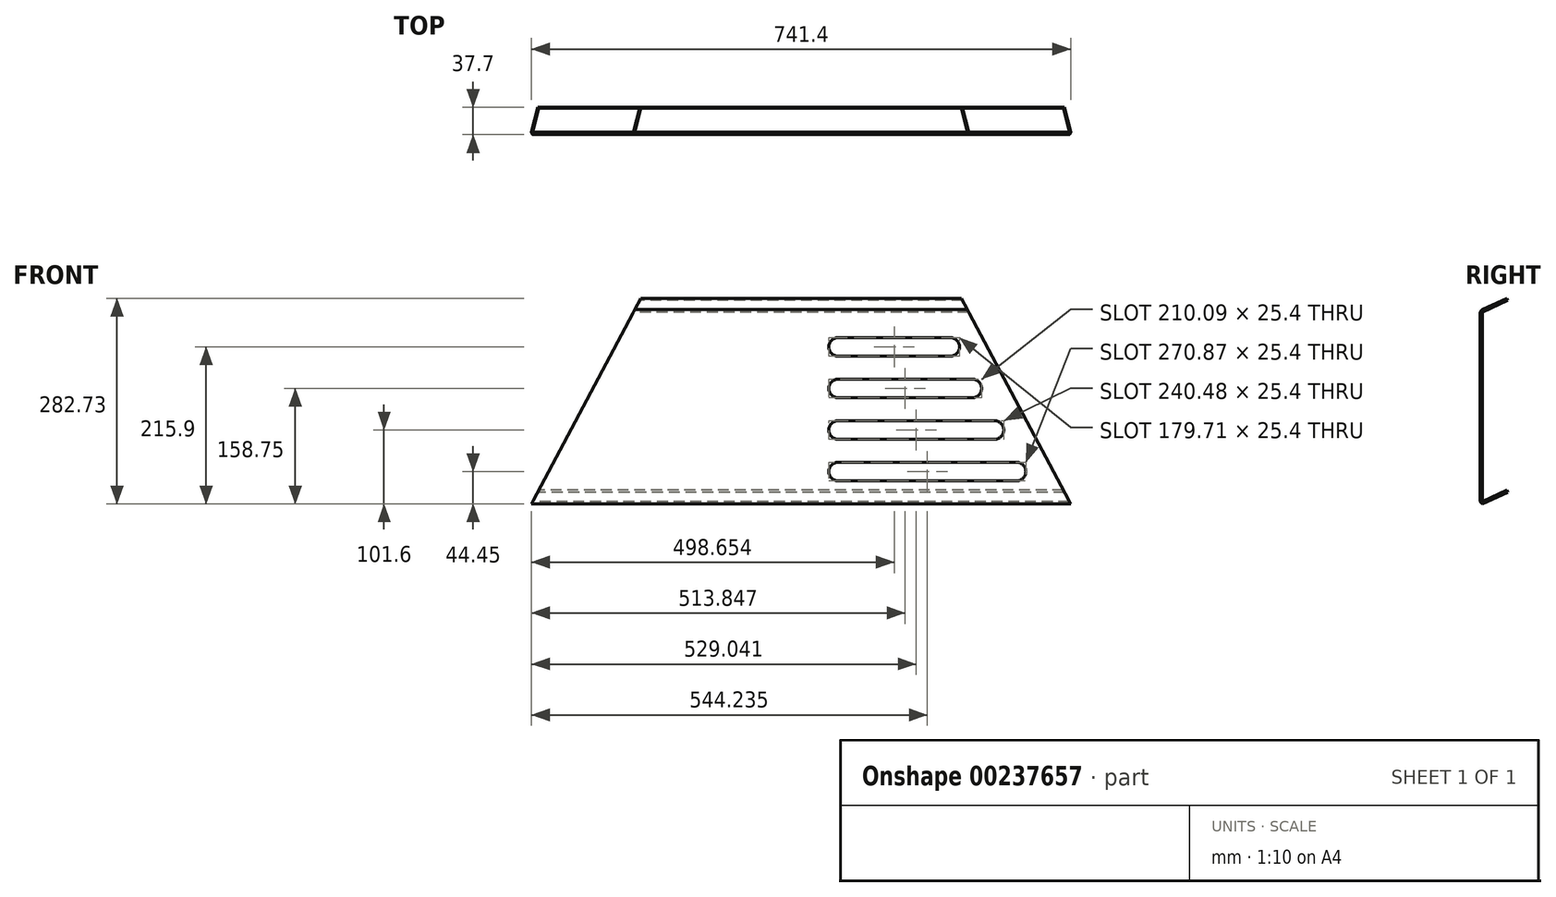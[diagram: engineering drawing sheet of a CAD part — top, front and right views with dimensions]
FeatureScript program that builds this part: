
annotation { "Feature Type Name" : "Feature", "Feature Type Description" : "" }
export const myFeature = defineFeature(function(context is Context, id is Id, definition is map)
    precondition{}
    {
        {
            var Q0;
            Q0=qCreatedBy(makeId("Front.planeOp"),FACE);
            var sketch = newSketch(context, id + "F0", { "sketchPlane" : qUnion([Q0])});
            skLineSegment(sketch, "E0", {"start": v(-228.6, 267.26) * mm, "end": v(228.6, 267.26) * mm});
            skLineSegment(sketch, "E1", {"start": v(228.6, 267.26) * mm, "end": v(370.7, 0) * mm});
            skLineSegment(sketch, "E2", {"start": v(370.7, 0) * mm, "end": v(-370.7, 0) * mm});
            skLineSegment(sketch, "E3", {"start": v(-370.7, 0) * mm, "end": v(-228.6, 267.26) * mm});
            skSolve(sketch);
        }
        {
            var Q0;
            Q0 = qSketchRegion(id + "F0", true);
            extrude(context, id + "F1", {"entities" : qUnion([Q0]), "depth" : 3.17 * mm});
        }
        {
            var Q0;
            Q0=qCreatedBy(makeId("Right.planeOp"),FACE);
            var sketch = newSketch(context, id + "F2", { "sketchPlane" : qUnion([Q0])});
            skLineSegment(sketch, "E4", {"start": v(0, 0) * mm, "end": v(34.53, 16.1) * mm});
            skLineSegment(sketch, "E5", {"start": v(34.53, 16.1) * mm, "end": v(33.19, 18.98) * mm});
            skLineSegment(sketch, "E6", {"start": v(33.19, 18.98) * mm, "end": v(0, 3.5) * mm});
            skLineSegment(sketch, "E7", {"start": v(0, 0) * mm, "end": v(0, 3.5) * mm});
            skLineSegment(sketch, "E8", {"start": v(0, 263.76) * mm, "end": v(34.53, 279.86) * mm});
            skLineSegment(sketch, "E9", {"start": v(34.53, 279.86) * mm, "end": v(33.19, 282.73) * mm});
            skLineSegment(sketch, "E10", {"start": v(33.19, 282.73) * mm, "end": v(0, 267.26) * mm});
            skLineSegment(sketch, "E11", {"start": v(0, 263.76) * mm, "end": v(0, 267.26) * mm});
            skSolve(sketch);
        }
        {
            var Q0;
            Q0=makeQuery(id+"F2.imprint","IMPRINT",FACE,{"disambiguationData":[TD([[makeQuery(id+"F2.imprint","IMPRINT",EDGE,{"derivedFrom":sQuery(id+"F2.wireOp",EDGE,"E4")}),1.0]])]});
            var Q1;
            Q1=makeQuery(id+"F2.imprint","IMPRINT",FACE,{"disambiguationData":[TD([[makeQuery(id+"F2.imprint","IMPRINT",EDGE,{"derivedFrom":sQuery(id+"F2.wireOp",EDGE,"E8")}),1.0]])]});
            var Q2;
            Q2=makeQuery(id+"F1.opExtrude","SWEPT_FACE",FACE,{"disambiguationData":[OSD([sQuery(id+"F0.wireOp",EDGE,"E1")])]});
            var Q3;
            Q3=makeQuery(id+"F1.opExtrude","SWEPT_FACE",FACE,{"disambiguationData":[OSD([sQuery(id+"F0.wireOp",EDGE,"E3")])]});
            extrude(context, id + "F3", {"entities" : qUnion([Q0, Q1]), "operationType" : NewBodyOperationType.ADD, "endBound" : BoundingType.UP_TO_SURFACE, "endBoundEntityFace" : qUnion([Q2]), "depth" : 25.4 * mm, "hasSecondDirection" : true, "secondDirectionBound" : SecondDirectionBoundingType.UP_TO_SURFACE, "secondDirectionOppositeDirection" : true, "secondDirectionBoundEntityFace" : qUnion([Q3]), "secondDirectionDepth" : 25.4 * mm});
        }
        {
            var Q0;
            Q0=makeQuery(id+"F1.opExtrude","CAP_FACE",FACE,{"disambiguationData":[OSD([sQuery(id+"F0.wireOp",EDGE,"E0"),sQuery(id+"F0.wireOp",EDGE,"E1"),sQuery(id+"F0.wireOp",EDGE,"E2"),sQuery(id+"F0.wireOp",EDGE,"E3")])],"isStart":false});
            var sketch = newSketch(context, id + "F4", { "sketchPlane" : qUnion([Q0])});
            skArc(sketch, "E12.0.startCap", {"start": v(50.8, 203.2) * mm, "mid": v(38.1, 215.9) * mm, "end": v(50.8, 228.6) * mm});
            skArc(sketch, "E12.0.endCap", {"start": v(205.1, 228.6) * mm, "mid": v(217.8, 215.9) * mm, "end": v(205.1, 203.2) * mm});
            skLineSegment(sketch, "E12.0.left", {"start": v(50.8, 228.6) * mm, "end": v(205.1, 228.6) * mm});
            skLineSegment(sketch, "E12.0.right", {"start": v(50.8, 203.2) * mm, "end": v(205.1, 203.2) * mm});
            skArc(sketch, "E13.0.startCap", {"start": v(50.8, 146.05) * mm, "mid": v(38.1, 158.75) * mm, "end": v(50.8, 171.45) * mm});
            skArc(sketch, "E13.0.endCap", {"start": v(235.5, 171.45) * mm, "mid": v(248.2, 158.75) * mm, "end": v(235.5, 146.05) * mm});
            skLineSegment(sketch, "E13.0.left", {"start": v(50.8, 171.45) * mm, "end": v(235.5, 171.45) * mm});
            skLineSegment(sketch, "E13.0.right", {"start": v(50.8, 146.05) * mm, "end": v(235.5, 146.05) * mm});
            skArc(sketch, "E13.1.startCap", {"start": v(50.8, 88.9) * mm, "mid": v(38.1, 101.6) * mm, "end": v(50.8, 114.3) * mm});
            skArc(sketch, "E13.1.endCap", {"start": v(265.88, 114.3) * mm, "mid": v(278.58, 101.6) * mm, "end": v(265.88, 88.9) * mm});
            skLineSegment(sketch, "E13.1.left", {"start": v(50.8, 114.3) * mm, "end": v(265.88, 114.3) * mm});
            skLineSegment(sketch, "E13.1.right", {"start": v(50.8, 88.9) * mm, "end": v(265.88, 88.9) * mm});
            skArc(sketch, "E13.2.startCap", {"start": v(50.8, 31.75) * mm, "mid": v(38.1, 44.45) * mm, "end": v(50.8, 57.15) * mm});
            skArc(sketch, "E13.2.endCap", {"start": v(296.27, 57.15) * mm, "mid": v(308.97, 44.45) * mm, "end": v(296.27, 31.75) * mm});
            skLineSegment(sketch, "E13.2.left", {"start": v(50.8, 57.15) * mm, "end": v(296.27, 57.15) * mm});
            skLineSegment(sketch, "E13.2.right", {"start": v(50.8, 31.75) * mm, "end": v(296.27, 31.75) * mm});
            skLineSegment(sketch, "E14", {"start": v(50.8, 215.9) * mm, "end": v(50.8, 0) * mm, "construction": true});
            skLineSegment(sketch, "E15", {"start": v(205.1, 215.9) * mm, "end": v(319.9, 0) * mm, "construction": true});
            skSolve(sketch);
        }
        {
            var Q0;
            Q0 = qSketchRegion(id + "F4", true);
            var Q1;
            Q1=makeQuery(id+"F1.opExtrude","CAP_FACE",FACE,{"disambiguationData":[OSD([sQuery(id+"F0.wireOp",EDGE,"E0"),sQuery(id+"F0.wireOp",EDGE,"E1"),sQuery(id+"F0.wireOp",EDGE,"E2"),sQuery(id+"F0.wireOp",EDGE,"E3")])],"isStart":true});
            extrude(context, id + "F5", {"entities" : qUnion([Q0]), "operationType" : NewBodyOperationType.REMOVE, "endBound" : BoundingType.UP_TO_SURFACE, "oppositeDirection" : true, "endBoundEntityFace" : qUnion([Q1]), "depth" : 25.4 * mm});
        }
        {
            var Q0;
            Q0=makeQuery(id+"F1.opExtrude","CAP_EDGE",EDGE,{"disambiguationData":[OSD([sQuery(id+"F0.wireOp",EDGE,"E0")])],"isStart":false});
            var Q1;
            Q1=makeQuery(id+"F1.opExtrude","CAP_EDGE",EDGE,{"disambiguationData":[OSD([sQuery(id+"F0.wireOp",EDGE,"E2")])],"isStart":false});
            fillet(context, id + "F6", {"entities" : qUnion([Q0, Q1]), "radius" : 5.08 * mm, "tangentPropagation" : true, "allowEdgeOverflow" : false});
        }
    });
